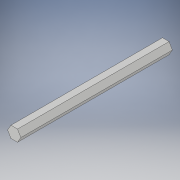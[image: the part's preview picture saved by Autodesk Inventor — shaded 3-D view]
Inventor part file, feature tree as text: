
AUTODESK INVENTOR PART (.ipt)
format: ipt  version: 2018 (Build 220112000, 112)  size: 94,208 bytes
history: native  units: in
note: dims shown in document units (in); Inventor stores cm internally (conversion verified against a paired STEP export)
features: extrude x1, sketch x1
ambient origin geometry x8: Origin, YZ Plane, XZ Plane, XY Plane, X Axis, Y Axis, Z Axis, Center Point
bodies: Solid1 (feature_tree)
feature tree (2):
  extrude  "Extrusion1"  Depth=6.625in TaperAngle=0.0deg
  sketch  "Sketch1"  dims[d0=0.5in d1=6.625in d2=0.0in]
